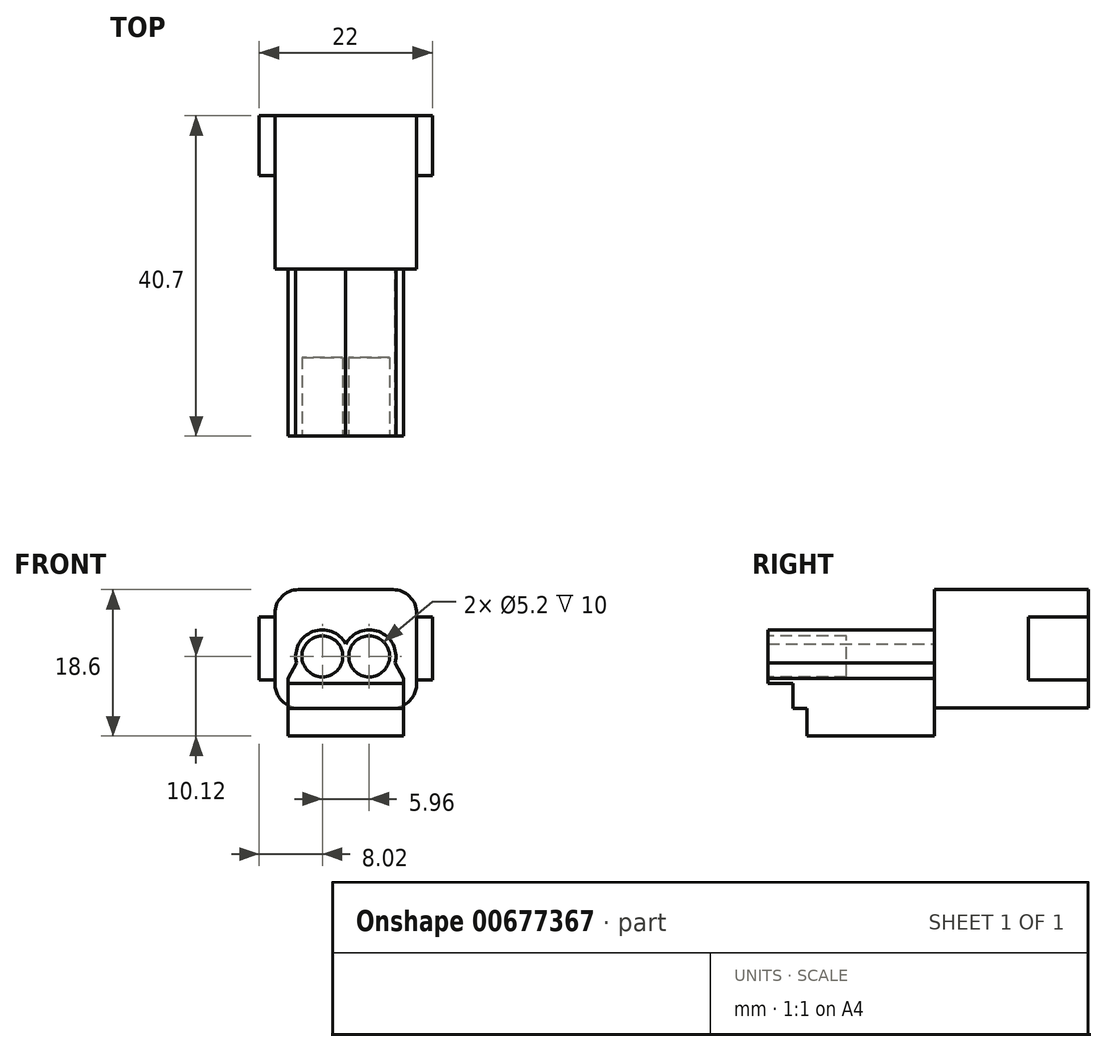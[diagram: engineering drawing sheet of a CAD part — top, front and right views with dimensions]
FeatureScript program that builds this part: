
annotation { "Feature Type Name" : "Feature", "Feature Type Description" : "" }
export const myFeature = defineFeature(function(context is Context, id is Id, definition is map)
    precondition{}
    {
        {
            var Q0;
            Q0=qCreatedBy(makeId("Front.planeOp"),FACE);
            var sketch = newSketch(context, id + "F0", { "sketchPlane" : qUnion([Q0])});
            skLineSegment(sketch, "E0.top", {"start": v(-7.35, -7.15) * mm, "end": v(7.35, -7.15) * mm});
            skLineSegment(sketch, "E0.left", {"start": v(-7.35, 0.2) * mm, "end": v(-7.35, -7.15) * mm});
            skLineSegment(sketch, "E0.right", {"start": v(7.35, 0.2) * mm, "end": v(7.35, -7.15) * mm});
            skPoint(sketch, "E0.middle", {"position": v(0, 0) * mm});
            skArc(sketch, "E1", {"start": v(0, 1.38) * mm, "mid": v(6.36, 2.97) * mm, "end": v(0, 4.56) * mm});
            skArc(sketch, "E2.MirrorC", {"start": v(0, 1.38) * mm, "mid": v(-6.36, 2.97) * mm, "end": v(0, 4.56) * mm});
            skLineSegment(sketch, "E3", {"start": v(6.26, 2.16) * mm, "end": v(7.35, 0.2) * mm});
            skLineSegment(sketch, "E4.MirrorCS", {"start": v(-6.26, 2.16) * mm, "end": v(-7.35, 0.2) * mm});
            skPoint(sketch, "E5.orphan", {"position": v(-7.35, 7.15) * mm});
            skPoint(sketch, "E6.orphan", {"position": v(7.35, 7.15) * mm});
            skSolve(sketch);
        }
        {
            var Q0;
            Q0 = qSketchRegion(id + "F0", true);
            extrude(context, id + "F1", {"entities" : qUnion([Q0]), "depth" : 21.2 * mm, "offsetDistance" : 25 * mm});
        }
        {
            var Q0;
            Q0=makeQuery(id+"F1.opExtrude","SWEPT_FACE",FACE,{"disambiguationData":[OSD([sQuery(id+"F0.wireOp",EDGE,"E0.top")])]});
            var sketch = newSketch(context, id + "F2", { "sketchPlane" : qUnion([Q0])});
            skLineSegment(sketch, "E7.bottom", {"start": v(-7.35, 21.2) * mm, "end": v(7.35, 21.2) * mm});
            skLineSegment(sketch, "E7.top", {"start": v(-7.35, 18) * mm, "end": v(7.35, 18) * mm});
            skLineSegment(sketch, "E7.left", {"start": v(-7.35, 21.2) * mm, "end": v(-7.35, 18) * mm});
            skLineSegment(sketch, "E7.right", {"start": v(7.35, 21.2) * mm, "end": v(7.35, 18) * mm});
            skSolve(sketch);
        }
        {
            var Q0;
            Q0 = qSketchRegion(id + "F2", true);
            extrude(context, id + "F3", {"entities" : qUnion([Q0]), "operationType" : NewBodyOperationType.REMOVE, "oppositeDirection" : true, "depth" : 6.7 * mm, "offsetDistance" : 25 * mm});
        }
        {
            var Q0;
            Q0=makeQuery(id+"F1.opExtrude","CAP_FACE",FACE,{"disambiguationData":[OSD([sQuery(id+"F0.wireOp",EDGE,"E0.top"),sQuery(id+"F0.wireOp",EDGE,"E0.left"),sQuery(id+"F0.wireOp",EDGE,"E0.right"),sQuery(id+"F0.wireOp",EDGE,"E1"),sQuery(id+"F0.wireOp",EDGE,"E2.MirrorC"),sQuery(id+"F0.wireOp",EDGE,"E3"),sQuery(id+"F0.wireOp",EDGE,"E4.MirrorCS")])],"isStart":false});
            var sketch = newSketch(context, id + "F4", { "sketchPlane" : qUnion([Q0])});
            skCircle(sketch, "E8", {"center": v(-2.98, 2.97) * mm, "radius": 2.6 * mm});
            skCircle(sketch, "E9", {"center": v(2.98, 2.97) * mm, "radius": 2.6 * mm});
            skSolve(sketch);
        }
        {
            var Q0;
            Q0 = qSketchRegion(id + "F4", true);
            extrude(context, id + "F5", {"entities" : qUnion([Q0]), "operationType" : NewBodyOperationType.REMOVE, "oppositeDirection" : true, "depth" : 10 * mm, "offsetDistance" : 25 * mm});
        }
        {
            var Q0;
            Q0=makeQuery(id+"F1.opExtrude","CAP_FACE",FACE,{"disambiguationData":[OSD([sQuery(id+"F0.wireOp",EDGE,"E0.top"),sQuery(id+"F0.wireOp",EDGE,"E0.left"),sQuery(id+"F0.wireOp",EDGE,"E0.right"),sQuery(id+"F0.wireOp",EDGE,"E1"),sQuery(id+"F0.wireOp",EDGE,"E2.MirrorC"),sQuery(id+"F0.wireOp",EDGE,"E3"),sQuery(id+"F0.wireOp",EDGE,"E4.MirrorCS")])],"isStart":true});
            var sketch = newSketch(context, id + "F6", { "sketchPlane" : qUnion([Q0])});
            skLineSegment(sketch, "E10.bottom", {"start": v(-9, -3.55) * mm, "end": v(9, -3.55) * mm});
            skLineSegment(sketch, "E10.top", {"start": v(-9, 11.45) * mm, "end": v(9, 11.45) * mm});
            skLineSegment(sketch, "E10.left", {"start": v(-9, -3.55) * mm, "end": v(-9, 11.45) * mm});
            skLineSegment(sketch, "E10.right", {"start": v(9, -3.55) * mm, "end": v(9, 11.45) * mm});
            skSolve(sketch);
        }
        {
            var Q0;
            Q0 = qSketchRegion(id + "F6", true);
            extrude(context, id + "F7", {"entities" : qUnion([Q0]), "operationType" : NewBodyOperationType.ADD, "depth" : 11.9 * mm, "offsetDistance" : 25 * mm});
        }
        {
            var Q0;
            Q0=makeQuery(id+"F7.opExtrude","CAP_FACE",FACE,{"disambiguationData":[OSD([sQuery(id+"F6.wireOp",EDGE,"E10.bottom"),sQuery(id+"F6.wireOp",EDGE,"E10.top"),sQuery(id+"F6.wireOp",EDGE,"E10.left"),sQuery(id+"F6.wireOp",EDGE,"E10.right")])],"isStart":false});
            var sketch = newSketch(context, id + "F8", { "sketchPlane" : qUnion([Q0])});
            skLineSegment(sketch, "E11.0.0", {"start": v(-9, -3.55) * mm, "end": v(9, -3.55) * mm});
            skLineSegment(sketch, "E11.0.1", {"start": v(9, -3.55) * mm, "end": v(9, -0.05) * mm});
            skLineSegment(sketch, "E11.0.2", {"start": v(9, 11.45) * mm, "end": v(-9, 11.45) * mm});
            skLineSegment(sketch, "E11.0.3", {"start": v(-9, 11.45) * mm, "end": v(-9, 7.95) * mm});
            skLineSegment(sketch, "E12.bottom", {"start": v(-9, 7.95) * mm, "end": v(-11, 7.95) * mm});
            skLineSegment(sketch, "E12.top", {"start": v(-9, -0.05) * mm, "end": v(-11, -0.05) * mm});
            skLineSegment(sketch, "E12.right", {"start": v(-11, 7.95) * mm, "end": v(-11, -0.05) * mm});
            skLineSegment(sketch, "E13.trimOffspring", {"start": v(-9, -0.05) * mm, "end": v(-9, -3.55) * mm});
            skLineSegment(sketch, "E14.MirrorCS", {"start": v(9, 7.95) * mm, "end": v(11, 7.95) * mm});
            skLineSegment(sketch, "E15.MirrorCS", {"start": v(11, 7.95) * mm, "end": v(11, -0.05) * mm});
            skLineSegment(sketch, "E16.MirrorCS", {"start": v(9, -0.05) * mm, "end": v(11, -0.05) * mm});
            skLineSegment(sketch, "E17.trimOffspring", {"start": v(9, 7.95) * mm, "end": v(9, 11.45) * mm});
            skSolve(sketch);
        }
        {
            var Q0;
            Q0 = qSketchRegion(id + "F8", true);
            extrude(context, id + "F9", {"entities" : qUnion([Q0]), "operationType" : NewBodyOperationType.ADD, "depth" : 7.6 * mm, "offsetDistance" : 25 * mm});
        }
        {
            var Q0;
            Q0=makeQuery(id+"F9.boolean.opBoolean","MERGE",EDGE,{"derivedFrom":[makeQuery(id+"F7.opExtrude","SWEPT_EDGE",EDGE,{"disambiguationData":[OSD([sQuery(id+"F6.wireOp",EDGE,"E10.top"),sQuery(id+"F6.wireOp",EDGE,"E10.left")])]}),makeQuery(id+"F9.opExtrude","SWEPT_EDGE",EDGE,{"disambiguationData":[OSD([sQuery(id+"F8.wireOp",EDGE,"E11.0.2"),sQuery(id+"F8.wireOp",EDGE,"E11.0.3")])]})]});
            var Q1;
            Q1=makeQuery(id+"F9.boolean.opBoolean","MERGE",EDGE,{"derivedFrom":[makeQuery(id+"F7.opExtrude","SWEPT_EDGE",EDGE,{"disambiguationData":[OSD([sQuery(id+"F6.wireOp",EDGE,"E10.top"),sQuery(id+"F6.wireOp",EDGE,"E10.right")])]}),makeQuery(id+"F9.opExtrude","SWEPT_EDGE",EDGE,{"disambiguationData":[OSD([sQuery(id+"F8.wireOp",EDGE,"E11.0.2"),sQuery(id+"F8.wireOp",EDGE,"E17.trimOffspring")])]})]});
            var Q2;
            Q2=makeQuery(id+"F9.boolean.opBoolean","MERGE",EDGE,{"derivedFrom":[makeQuery(id+"F7.opExtrude","SWEPT_EDGE",EDGE,{"disambiguationData":[OSD([sQuery(id+"F6.wireOp",EDGE,"E10.bottom"),sQuery(id+"F6.wireOp",EDGE,"E10.left")])]}),makeQuery(id+"F9.opExtrude","SWEPT_EDGE",EDGE,{"disambiguationData":[OSD([sQuery(id+"F8.wireOp",EDGE,"E11.0.0"),sQuery(id+"F8.wireOp",EDGE,"E13.trimOffspring")])]})]});
            var Q3;
            Q3=makeQuery(id+"F9.boolean.opBoolean","MERGE",EDGE,{"derivedFrom":[makeQuery(id+"F7.opExtrude","SWEPT_EDGE",EDGE,{"disambiguationData":[OSD([sQuery(id+"F6.wireOp",EDGE,"E10.bottom"),sQuery(id+"F6.wireOp",EDGE,"E10.right")])]}),makeQuery(id+"F9.opExtrude","SWEPT_EDGE",EDGE,{"disambiguationData":[OSD([sQuery(id+"F8.wireOp",EDGE,"E11.0.0"),sQuery(id+"F8.wireOp",EDGE,"E11.0.1")])]})]});
            fillet(context, id + "F10", {"entities" : qUnion([Q0, Q1, Q2, Q3]), "radius" : 3 * mm, "tangentPropagation" : true, "allowEdgeOverflow" : false});
        }
        {
            var Q0;
            Q0=makeQuery(id+"F1.opExtrude","SWEPT_FACE",FACE,{"disambiguationData":[OSD([sQuery(id+"F0.wireOp",EDGE,"E0.top")])]});
            var sketch = newSketch(context, id + "F11", { "sketchPlane" : qUnion([Q0])});
            skLineSegment(sketch, "E18.bottom", {"start": v(7.35, 18) * mm, "end": v(-7.35, 18) * mm});
            skLineSegment(sketch, "E18.top", {"start": v(7.35, 16.2) * mm, "end": v(-7.35, 16.2) * mm});
            skLineSegment(sketch, "E18.left", {"start": v(7.35, 18) * mm, "end": v(7.35, 16.2) * mm});
            skLineSegment(sketch, "E18.right", {"start": v(-7.35, 18) * mm, "end": v(-7.35, 16.2) * mm});
            skSolve(sketch);
        }
        {
            var Q0;
            Q0 = qSketchRegion(id + "F11", true);
            extrude(context, id + "F12", {"entities" : qUnion([Q0]), "operationType" : NewBodyOperationType.REMOVE, "oppositeDirection" : true, "depth" : 3.5 * mm, "offsetDistance" : 25 * mm});
        }
    });
